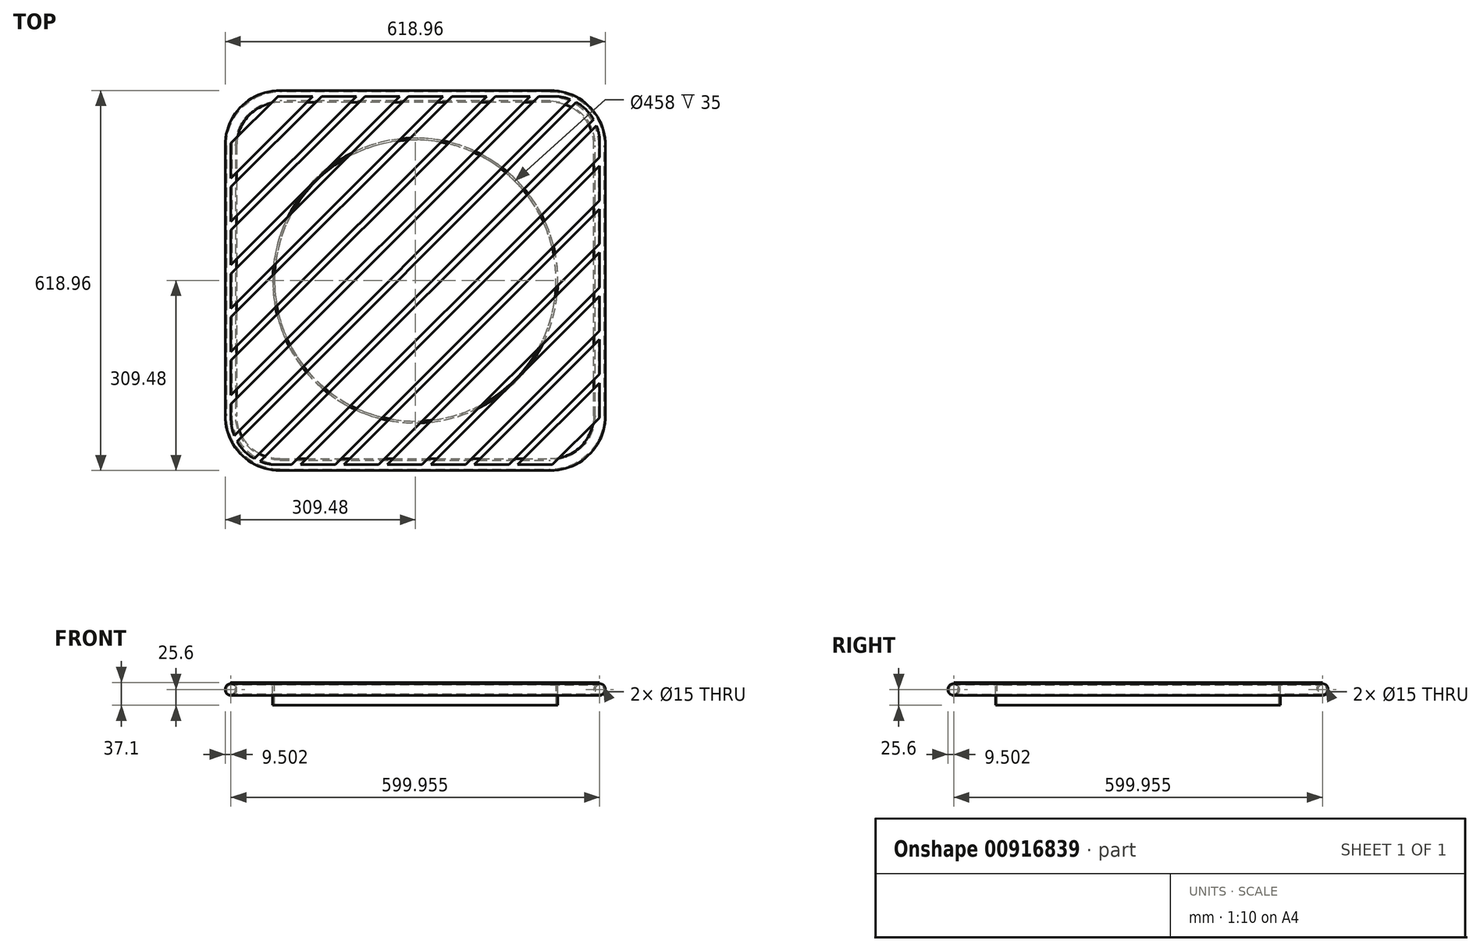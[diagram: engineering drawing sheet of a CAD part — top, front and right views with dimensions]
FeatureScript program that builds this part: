
annotation { "Feature Type Name" : "Feature", "Feature Type Description" : "" }
export const myFeature = defineFeature(function(context is Context, id is Id, definition is map)
    precondition{}
    {
        {
            var Q0;
            Q0=qCreatedBy(makeId("Top.planeOp"),FACE);
            var sketch = newSketch(context, id + "F0", { "sketchPlane" : qUnion([Q0])});
            skLineSegment(sketch, "E0.bottom", {"start": v(-220, 300) * mm, "end": v(220, 300) * mm});
            skLineSegment(sketch, "E0.top", {"start": v(-220, -300) * mm, "end": v(220, -300) * mm});
            skLineSegment(sketch, "E0.left", {"start": v(-300, 220) * mm, "end": v(-300, -220) * mm});
            skLineSegment(sketch, "E0.right", {"start": v(300, 220) * mm, "end": v(300, -220) * mm});
            skPoint(sketch, "E0.middle", {"position": v(0, 0) * mm});
            skArc(sketch, "E1", {"start": v(-220, 300) * mm, "mid": v(-276.57, 276.57) * mm, "end": v(-300, 220) * mm});
            skArc(sketch, "E2", {"start": v(300, 220) * mm, "mid": v(276.57, 276.57) * mm, "end": v(220, 300) * mm});
            skPoint(sketch, "E3.orphan", {"position": v(-300, 300) * mm});
            skPoint(sketch, "E4.orphan", {"position": v(300, 300) * mm});
            skArc(sketch, "E5.MirrorCS", {"start": v(300, -220) * mm, "mid": v(276.57, -276.57) * mm, "end": v(220, -300) * mm});
            skArc(sketch, "E6.MirrorCS", {"start": v(-220, -300) * mm, "mid": v(-276.57, -276.57) * mm, "end": v(-300, -220) * mm});
            skPoint(sketch, "E7.orphan", {"position": v(-300, -300) * mm});
            skPoint(sketch, "E8.orphan", {"position": v(300, -300) * mm});
            skSolve(sketch);
        }
        {
            var Q0;
            Q0=qCreatedBy(makeId("Front.planeOp"),FACE);
            var sketch = newSketch(context, id + "F1", { "sketchPlane" : qUnion([Q0])});
            skCircle(sketch, "E9", {"center": v(-299.98, 0) * mm, "radius": 9.5 * mm});
            skCircle(sketch, "E10", {"center": v(-299.98, 0) * mm, "radius": 7.5 * mm});
            skSolve(sketch);
        }
        {
            var Q0;
            Q0=makeQuery(id+"F1.imprint","IMPRINT",FACE,{"disambiguationData":[TD([[makeQuery(id+"F1.imprint","IMPRINT",EDGE,{"derivedFrom":sQuery(id+"F1.wireOp",EDGE,"E9")}),1.0]])]});
            var Q1;
            Q1=sQuery(id+"F0.wireOp",EDGE,"E0.left");
            var Q2;
            Q2=sQuery(id+"F0.wireOp",EDGE,"E1");
            var Q3;
            Q3=sQuery(id+"F0.wireOp",EDGE,"E0.bottom");
            var Q4;
            Q4=sQuery(id+"F0.wireOp",EDGE,"E2");
            var Q5;
            Q5=sQuery(id+"F0.wireOp",EDGE,"E0.right");
            var Q6;
            Q6=sQuery(id+"F0.wireOp",EDGE,"E5.MirrorCS");
            var Q7;
            Q7=sQuery(id+"F0.wireOp",EDGE,"E0.top");
            var Q8;
            Q8=sQuery(id+"F0.wireOp",EDGE,"E6.MirrorCS");
            sweep(context, id + "F2", {"profiles" : qUnion([Q0]), "path" : qUnion([Q1, Q2, Q3, Q4, Q5, Q6, Q7, Q8])});
        }
        {
            var Q0;
            Q0=qCreatedBy(makeId("Top.planeOp"),FACE);
            cPlane(context, id + "F3", {"entities" : qUnion([Q0]), "cplaneType" : CPlaneType.OFFSET, "offset" : 9.5 * mm, "width" : 150 * mm, "height" : 150 * mm});
        }
        {
            var Q0;
            Q0=qCreatedBy(id+"F3.planeOp",FACE);
            var sketch = newSketch(context, id + "F4", { "sketchPlane" : qUnion([Q0])});
            skLineSegment(sketch, "E11.bottom", {"start": v(-225, 300) * mm, "end": v(225, 300) * mm});
            skLineSegment(sketch, "E11.top", {"start": v(-225, -300) * mm, "end": v(225, -300) * mm});
            skLineSegment(sketch, "E11.left", {"start": v(-300, 225) * mm, "end": v(-300, -225) * mm});
            skLineSegment(sketch, "E11.right", {"start": v(300, 225) * mm, "end": v(300, -225) * mm});
            skPoint(sketch, "E11.middle", {"position": v(0, 0) * mm});
            skArc(sketch, "E12", {"start": v(-225, 300) * mm, "mid": v(-278.03, 278.03) * mm, "end": v(-300, 225) * mm});
            skArc(sketch, "E13", {"start": v(300, 225) * mm, "mid": v(278.03, 278.03) * mm, "end": v(225, 300) * mm});
            skPoint(sketch, "E14.orphan", {"position": v(-300, 300) * mm});
            skPoint(sketch, "E15.orphan", {"position": v(300, 300) * mm});
            skArc(sketch, "E16.MirrorCS", {"start": v(-225, -300) * mm, "mid": v(-278.03, -278.03) * mm, "end": v(-300, -225) * mm});
            skArc(sketch, "E17.MirrorCS", {"start": v(300, -225) * mm, "mid": v(278.03, -278.03) * mm, "end": v(225, -300) * mm});
            skPoint(sketch, "E18.orphan", {"position": v(-300, -300) * mm});
            skPoint(sketch, "E19.orphan", {"position": v(300, -300) * mm});
            skLineSegment(sketch, "E20", {"start": v(-300, 11.13) * mm, "end": v(-11.13, 300) * mm});
            skLineSegment(sketch, "E21", {"start": v(45.44, 300) * mm, "end": v(-300, -45.44) * mm});
            skLineSegment(sketch, "E22", {"start": v(59.58, 300) * mm, "end": v(-300, -59.58) * mm});
            skLineSegment(sketch, "E23", {"start": v(116.15, 300) * mm, "end": v(-300, -116.15) * mm});
            skLineSegment(sketch, "E24", {"start": v(130.3, 300) * mm, "end": v(-300, -130.3) * mm});
            skLineSegment(sketch, "E25", {"start": v(186.86, 300) * mm, "end": v(-300, -186.86) * mm});
            skLineSegment(sketch, "E26", {"start": v(201, 300) * mm, "end": v(-300, -201) * mm});
            skLineSegment(sketch, "E27", {"start": v(257.57, 300) * mm, "end": v(-300, -257.57) * mm});
            skLineSegment(sketch, "E28", {"start": v(-290.25, -261.97) * mm, "end": v(261.97, 290.25) * mm});
            skLineSegment(sketch, "E29.MirrorCS", {"start": v(-261.97, -290.25) * mm, "end": v(290.25, 261.97) * mm});
            skLineSegment(sketch, "E30.MirrorCS", {"start": v(294.82, 252.4) * mm, "end": v(-252.4, -294.82) * mm});
            skLineSegment(sketch, "E31.MirrorCS", {"start": v(300, 201) * mm, "end": v(-201, -300) * mm});
            skLineSegment(sketch, "E32.MirrorCS", {"start": v(300, 186.86) * mm, "end": v(-186.86, -300) * mm});
            skLineSegment(sketch, "E33.MirrorCS", {"start": v(300, 130.3) * mm, "end": v(-130.3, -300) * mm});
            skLineSegment(sketch, "E34.MirrorCS", {"start": v(300, 116.15) * mm, "end": v(-116.15, -300) * mm});
            skLineSegment(sketch, "E35.MirrorCS", {"start": v(300, 59.58) * mm, "end": v(-59.58, -300) * mm});
            skLineSegment(sketch, "E36.MirrorCS", {"start": v(300, 45.44) * mm, "end": v(-45.44, -300) * mm});
            skLineSegment(sketch, "E37.MirrorCS", {"start": v(11.13, -300) * mm, "end": v(300, -11.13) * mm});
            skLineSegment(sketch, "E38", {"start": v(300, -25.27) * mm, "end": v(25.27, -300) * mm});
            skLineSegment(sketch, "E39", {"start": v(300, -81.84) * mm, "end": v(81.84, -300) * mm});
            skLineSegment(sketch, "E40", {"start": v(300, -95.98) * mm, "end": v(95.98, -300) * mm});
            skLineSegment(sketch, "E41", {"start": v(-225, -225) * mm, "end": v(225, 225) * mm});
            skLineSegment(sketch, "E42", {"start": v(300, -152.55) * mm, "end": v(152.55, -300) * mm});
            skLineSegment(sketch, "E43.MirrorCS", {"start": v(-152.55, 300) * mm, "end": v(-300, 152.55) * mm});
            skLineSegment(sketch, "E44.MirrorCS", {"start": v(-95.98, 300) * mm, "end": v(-300, 95.98) * mm});
            skLineSegment(sketch, "E45.MirrorCS", {"start": v(-81.84, 300) * mm, "end": v(-300, 81.84) * mm});
            skLineSegment(sketch, "E46.MirrorCS", {"start": v(-25.27, 300) * mm, "end": v(-300, 25.27) * mm});
            skLineSegment(sketch, "E47", {"start": v(-166.7, 300) * mm, "end": v(-300, 166.7) * mm});
            skLineSegment(sketch, "E48", {"start": v(-223.26, 300) * mm, "end": v(-300, 223.26) * mm});
            skLineSegment(sketch, "E49.MirrorCS", {"start": v(300, -166.7) * mm, "end": v(166.7, -300) * mm});
            skLineSegment(sketch, "E50.MirrorCS", {"start": v(300, -223.26) * mm, "end": v(223.26, -300) * mm});
            skSolve(sketch);
        }
        {
            var Q0;
            {var subQ0=sQuery(id+"F4.wireOp",EDGE,"E20");Q0=makeQuery(id+"F4.imprint","IMPRINT",FACE,{"disambiguationData":[TD([[makeQuery(id+"F4.imprint","IMPRINT",EDGE,{"derivedFrom":subQ0}),-1.0]])]});}
            var Q1;
            {var subQ0=sQuery(id+"F4.wireOp",EDGE,"E22");Q1=makeQuery(id+"F4.imprint","IMPRINT",FACE,{"disambiguationData":[TD([[makeQuery(id+"F4.imprint","IMPRINT",EDGE,{"derivedFrom":subQ0}),1.0]])]});}
            var Q2;
            {var subQ0=sQuery(id+"F4.wireOp",EDGE,"E24");Q2=makeQuery(id+"F4.imprint","IMPRINT",FACE,{"disambiguationData":[TD([[makeQuery(id+"F4.imprint","IMPRINT",EDGE,{"derivedFrom":subQ0}),1.0]])]});}
            var Q3;
            {var subQ0=sQuery(id+"F4.wireOp",EDGE,"E26");Q3=makeQuery(id+"F4.imprint","IMPRINT",FACE,{"disambiguationData":[TD([[makeQuery(id+"F4.imprint","IMPRINT",EDGE,{"derivedFrom":subQ0}),1.0]])]});}
            var Q4;
            {var subQ0=sQuery(id+"F4.wireOp",EDGE,"f3e3acb9-5dc7-480f-a169-b6047dde436d0.MirrorCS");Q4=makeQuery(id+"F4.imprint","IMPRINT",FACE,{"disambiguationData":[TD([[makeQuery(id+"F4.imprint","IMPRINT",EDGE,{"derivedFrom":subQ0}),1.0]])]});}
            var Q5;
            {var subQ0=sQuery(id+"F4.wireOp",EDGE,"8c5f72dc-6430-4fd1-9669-a3bc66972e370.MirrorCS");Q5=makeQuery(id+"F4.imprint","IMPRINT",FACE,{"disambiguationData":[TD([[makeQuery(id+"F4.imprint","IMPRINT",EDGE,{"derivedFrom":subQ0}),1.0]])]});}
            var Q6;
            {var subQ0=sQuery(id+"F4.wireOp",EDGE,"5638e17f-524b-40a8-8cfa-9c4565ae56270.MirrorCS");Q6=makeQuery(id+"F4.imprint","IMPRINT",FACE,{"disambiguationData":[TD([[makeQuery(id+"F4.imprint","IMPRINT",EDGE,{"derivedFrom":subQ0}),1.0]])]});}
            var Q7;
            {var subQ0=sQuery(id+"F4.wireOp",EDGE,"d3d81764-08a6-4486-8bd4-b46154aa33660.MirrorCS");Q7=makeQuery(id+"F4.imprint","IMPRINT",FACE,{"disambiguationData":[TD([[makeQuery(id+"F4.imprint","IMPRINT",EDGE,{"derivedFrom":subQ0}),1.0]])]});}
            var Q8;
            {var subQ0=sQuery(id+"F4.wireOp",EDGE,"Kz8hN87C-jPTE-dKEJ-GhUn-43Xg0fKDj0rT");Q8=makeQuery(id+"F4.imprint","IMPRINT",FACE,{"disambiguationData":[TD([[makeQuery(id+"F4.imprint","IMPRINT",EDGE,{"derivedFrom":subQ0}),-1.0]])]});}
            var Q9;
            {var subQ0=sQuery(id+"F4.wireOp",EDGE,"E30.MirrorCS");Q9=makeQuery(id+"F4.imprint","IMPRINT",FACE,{"disambiguationData":[TD([[makeQuery(id+"F4.imprint","IMPRINT",EDGE,{"derivedFrom":subQ0}),1.0]])]});}
            var Q10;
            {var subQ0=sQuery(id+"F4.wireOp",EDGE,"E32.MirrorCS");Q10=makeQuery(id+"F4.imprint","IMPRINT",FACE,{"disambiguationData":[TD([[makeQuery(id+"F4.imprint","IMPRINT",EDGE,{"derivedFrom":subQ0}),1.0]])]});}
            var Q11;
            {var subQ0=sQuery(id+"F4.wireOp",EDGE,"E34.MirrorCS");Q11=makeQuery(id+"F4.imprint","IMPRINT",FACE,{"disambiguationData":[TD([[makeQuery(id+"F4.imprint","IMPRINT",EDGE,{"derivedFrom":subQ0}),1.0]])]});}
            var Q12;
            {var subQ0=sQuery(id+"F4.wireOp",EDGE,"E36.MirrorCS");Q12=makeQuery(id+"F4.imprint","IMPRINT",FACE,{"disambiguationData":[TD([[makeQuery(id+"F4.imprint","IMPRINT",EDGE,{"derivedFrom":subQ0}),1.0]])]});}
            var Q13;
            {var subQ0=sQuery(id+"F4.wireOp",EDGE,"E38");Q13=makeQuery(id+"F4.imprint","IMPRINT",FACE,{"disambiguationData":[TD([[makeQuery(id+"F4.imprint","IMPRINT",EDGE,{"derivedFrom":subQ0}),1.0]])]});}
            var Q14;
            {var subQ6=sQuery(id+"F4.wireOp",EDGE,"E40");Q14=makeQuery(id+"F4.imprint","IMPRINT",FACE,{"disambiguationData":[TD([[makeQuery(id+"F4.imprint","IMPRINT",EDGE,{"derivedFrom":subQ6}),1.0]])]});}
            var Q15;
            {var subQ0=sQuery(id+"F4.wireOp",EDGE,"E45.MirrorCS");Q15=makeQuery(id+"F4.imprint","IMPRINT",FACE,{"disambiguationData":[TD([[makeQuery(id+"F4.imprint","IMPRINT",EDGE,{"derivedFrom":subQ0}),1.0]])]});}
            var Q16;
            {var subQ3=sQuery(id+"F4.wireOp",EDGE,"E43.MirrorCS");Q16=makeQuery(id+"F4.imprint","IMPRINT",FACE,{"disambiguationData":[TD([[makeQuery(id+"F4.imprint","IMPRINT",EDGE,{"derivedFrom":subQ3}),1.0]])]});}
            var Q17;
            {var subQ0=sQuery(id+"F4.wireOp",EDGE,"E28");Q17=makeQuery(id+"F4.imprint","IMPRINT",FACE,{"disambiguationData":[TD([[makeQuery(id+"F4.imprint","IMPRINT",EDGE,{"derivedFrom":subQ0}),-1.0]])]});}
            var Q18;
            {var subQ7=sQuery(id+"F4.wireOp",EDGE,"E49.MirrorCS");Q18=makeQuery(id+"F4.imprint","IMPRINT",FACE,{"disambiguationData":[TD([[makeQuery(id+"F4.imprint","IMPRINT",EDGE,{"derivedFrom":subQ7}),1.0]])]});}
            var Q19;
            {var subQ8=sQuery(id+"F4.wireOp",EDGE,"E47");Q19=makeQuery(id+"F4.imprint","IMPRINT",FACE,{"disambiguationData":[TD([[makeQuery(id+"F4.imprint","IMPRINT",EDGE,{"derivedFrom":subQ8}),-1.0]])]});}
            extrude(context, id + "F5", {"entities" : qUnion([Q0, Q1, Q2, Q3, Q4, Q5, Q6, Q7, Q8, Q9, Q10, Q11, Q12, Q13, Q14, Q15, Q16, Q17, Q18, Q19]), "operationType" : NewBodyOperationType.ADD, "depth" : 2 * mm, "offsetDistance" : 25 * mm, "hasSecondDirection" : true, "secondDirectionOppositeDirection" : true, "secondDirectionDepth" : .1 * mm});
        }
        {
            var Q0;
            Q0=makeQuery(id+"F5.opExtrude","CAP_FACE",FACE,{"disambiguationData":[OSD([sQuery(id+"F4.wireOp",EDGE,"E11.top"),sQuery(id+"F4.wireOp",EDGE,"E11.right"),sQuery(id+"F4.wireOp",EDGE,"E34.MirrorCS"),sQuery(id+"F4.wireOp",EDGE,"E35.MirrorCS")])],"isStart":true});
            var sketch = newSketch(context, id + "F6", { "sketchPlane" : qUnion([Q0])});
            skCircle(sketch, "E51", {"center": v(0, 0) * mm, "radius": 229 * mm});
            skCircle(sketch, "E52", {"center": v(0, 0) * mm, "radius": 232 * mm});
            skSolve(sketch);
        }
        {
            var Q0;
            Q0=qSketchRegion(id+"F6",true);
            extrude(context, id + "F7", {"entities" : qUnion([Q0]), "operationType" : NewBodyOperationType.ADD, "depth" : 35 * mm, "offsetDistance" : 25 * mm});
        }
    });
